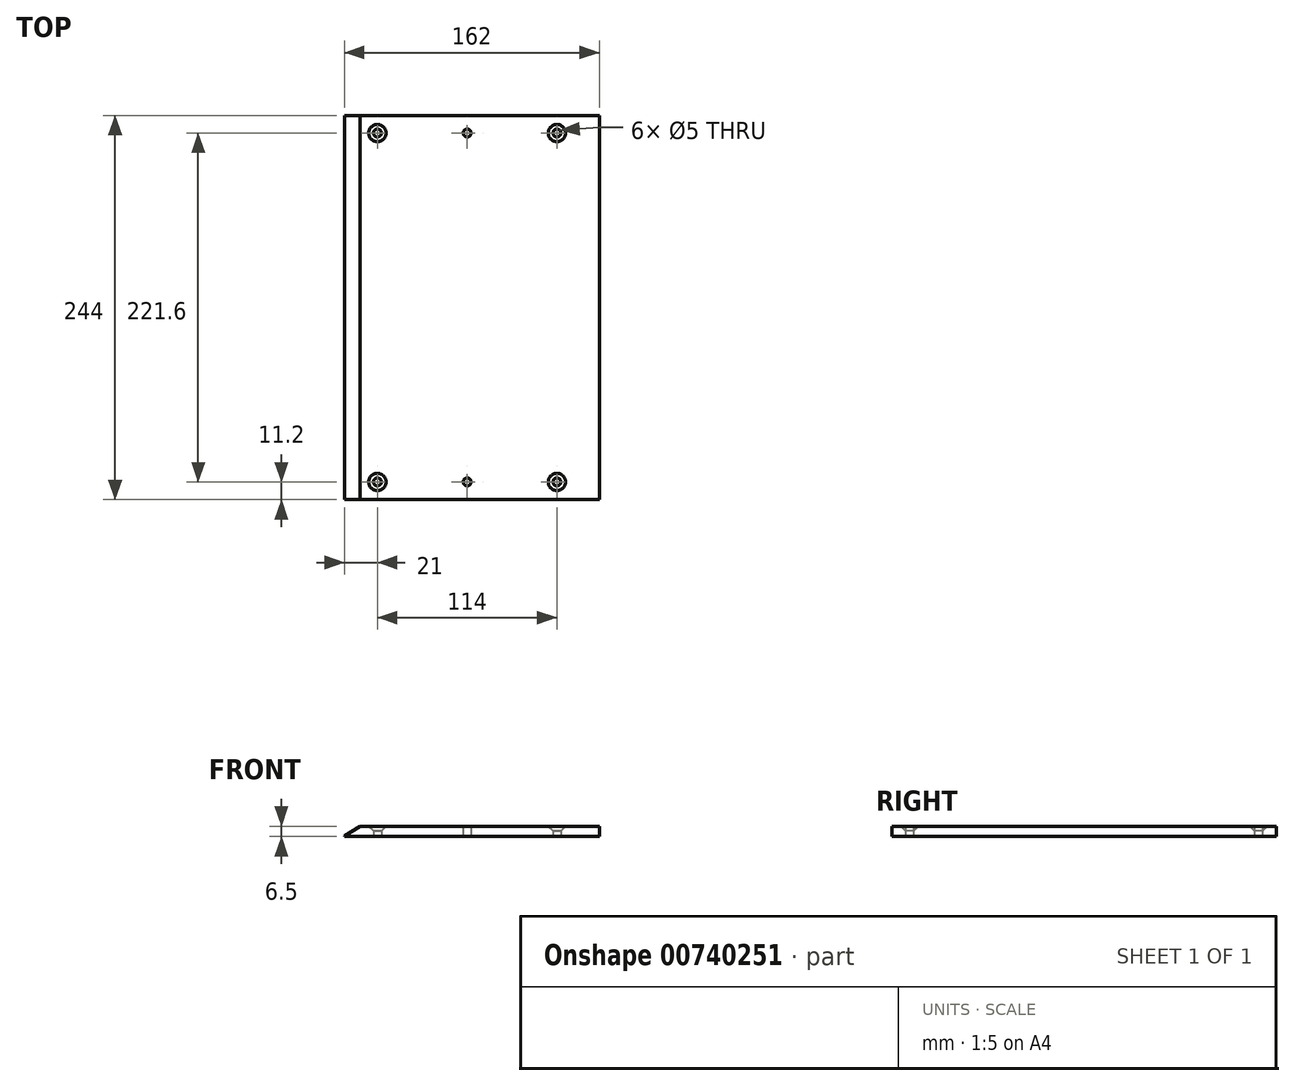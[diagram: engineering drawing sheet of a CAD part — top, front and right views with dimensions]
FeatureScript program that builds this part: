
annotation { "Feature Type Name" : "Feature", "Feature Type Description" : "" }
export const myFeature = defineFeature(function(context is Context, id is Id, definition is map)
    precondition{}
    {
        {
            var Q0;
            Q0=qCreatedBy(makeId("Top.planeOp"),FACE);
            var sketch = newSketch(context, id + "F0", { "sketchPlane" : qUnion([Q0])});
            skLineSegment(sketch, "E0.bottom", {"start": v(-120, 83.5) * mm, "end": v(120, 83.5) * mm});
            skLineSegment(sketch, "E0.top", {"start": v(-120, -83.5) * mm, "end": v(120, -83.5) * mm});
            skLineSegment(sketch, "E0.left", {"start": v(-120, 83.5) * mm, "end": v(-120, -83.5) * mm});
            skLineSegment(sketch, "E0.right", {"start": v(120, 83.5) * mm, "end": v(120, -83.5) * mm});
            skLineSegment(sketch, "E1", {"start": v(-109, 83.5) * mm, "end": v(-109, -83.5) * mm, "construction": true});
            skCircle(sketch, "E2", {"center": v(-109, -56.5) * mm, "radius": 2.5 * mm});
            skCircle(sketch, "E3", {"center": v(-109, -1) * mm, "radius": 2.5 * mm});
            skCircle(sketch, "E4", {"center": v(-109, 57.5) * mm, "radius": 2.5 * mm});
            skCircle(sketch, "E5.MirrorC", {"center": v(109, 57.5) * mm, "radius": 2.5 * mm});
            skCircle(sketch, "E6.MirrorC", {"center": v(109, -1) * mm, "radius": 2.5 * mm});
            skCircle(sketch, "E7.MirrorC", {"center": v(109, -56.5) * mm, "radius": 2.5 * mm});
            skCircle(sketch, "E8", {"center": v(-109, -56.5) * mm, "radius": 5.25 * mm});
            skCircle(sketch, "E9", {"center": v(-109, -1) * mm, "radius": 5.25 * mm});
            skCircle(sketch, "E10", {"center": v(-109, 57.5) * mm, "radius": 5.25 * mm});
            skCircle(sketch, "E11", {"center": v(109, 57.5) * mm, "radius": 5.25 * mm});
            skCircle(sketch, "E12", {"center": v(109, -1) * mm, "radius": 5.25 * mm});
            skCircle(sketch, "E13", {"center": v(109, -56.5) * mm, "radius": 5.25 * mm});
            skSolve(sketch);
        }
        {
            var Q0;
            Q0=qCreatedBy(makeId("Top.planeOp"),FACE);
            var sketch = newSketch(context, id + "F1", { "sketchPlane" : qUnion([Q0])});
            skLineSegment(sketch, "E14.0", {"start": v(-120, 83.5) * mm, "end": v(-120, -83.5) * mm});
            skLineSegment(sketch, "E15.0", {"start": v(-120, 83.5) * mm, "end": v(120, 83.5) * mm});
            skLineSegment(sketch, "E16.0", {"start": v(120, 83.5) * mm, "end": v(120, -83.5) * mm});
            skLineSegment(sketch, "E17.0", {"start": v(-120, -83.5) * mm, "end": v(120, -83.5) * mm});
            skSolve(sketch);
        }
        {
            var Q0;
            Q0 = qSketchRegion(id + "F1", true);
            extrude(context, id + "F2", {"entities" : qUnion([Q0]), "depth" : 6.5 * mm, "offsetDistance" : 25 * mm});
        }
        {
            var Q0;
            Q0=makeQuery(id+"F0.imprint","IMPRINT",FACE,{"disambiguationData":[TD([[makeQuery(id+"F0.imprint","IMPRINT",EDGE,{"derivedFrom":sQuery(id+"F0.wireOp",EDGE,"E0.bottom")}),-1.0]])]});
            var sketch = newSketch(context, id + "F3", { "sketchPlane" : qUnion([Q0])});
            skCircle(sketch, "E18.0", {"center": v(109, -56.5) * mm, "radius": 2.5 * mm, "construction": true});
            skLineSegment(sketch, "E19", {"start": v(110.8, 87.15) * mm, "end": v(110.8, -89.05) * mm, "construction": true});
            skCircle(sketch, "E20", {"center": v(110.8, -56.5) * mm, "radius": 2.5 * mm});
            skCircle(sketch, "E21.0", {"center": v(109, 57.5) * mm, "radius": 2.5 * mm, "construction": true});
            skCircle(sketch, "E22", {"center": v(110.8, 57.5) * mm, "radius": 2.5 * mm});
            skCircle(sketch, "E23.MirrorC", {"center": v(-110.8, -56.5) * mm, "radius": 2.5 * mm});
            skCircle(sketch, "E24.MirrorC", {"center": v(-110.8, 57.5) * mm, "radius": 2.5 * mm});
            skCircle(sketch, "E25", {"center": v(110.8, 0.5) * mm, "radius": 2.5 * mm});
            skCircle(sketch, "E26", {"center": v(-110.8, 0.5) * mm, "radius": 2.5 * mm});
            skLineSegment(sketch, "E27.0.0", {"start": v(-120, 83.5) * mm, "end": v(-120, -83.5) * mm, "construction": true});
            skLineSegment(sketch, "E27.0.1", {"start": v(-120, -83.5) * mm, "end": v(120, -83.5) * mm, "construction": true});
            skLineSegment(sketch, "E27.0.2", {"start": v(120, -83.5) * mm, "end": v(120, 83.5) * mm, "construction": true});
            skLineSegment(sketch, "E27.0.3", {"start": v(120, 83.5) * mm, "end": v(-120, 83.5) * mm, "construction": true});
            skSolve(sketch);
        }
        {
            var Q0;
            Q0 = qSketchRegion(id + "F3", true);
            extrude(context, id + "F4", {"entities" : qUnion([Q0]), "operationType" : NewBodyOperationType.REMOVE, "depth" : 25 * mm, "offsetDistance" : 25 * mm});
        }
        {
            var Q0;
            Q0=makeQuery(id+"F2.opExtrude","CAP_FACE",FACE,{"disambiguationData":[OSD([sQuery(id+"F1.wireOp",EDGE,"E14.0"),sQuery(id+"F1.wireOp",EDGE,"E15.0"),sQuery(id+"F1.wireOp",EDGE,"E16.0"),sQuery(id+"F1.wireOp",EDGE,"E17.0")])],"isStart":false});
            var sketch = newSketch(context, id + "F5", { "sketchPlane" : qUnion([Q0])});
            skCircle(sketch, "E28.0", {"center": v(110.8, -56.5) * mm, "radius": 2.5 * mm, "construction": true});
            skLineSegment(sketch, "E29", {"start": v(120, -29.5) * mm, "end": v(146.96, -29.5) * mm, "construction": true});
            skLineSegment(sketch, "E30", {"start": v(120, -83.5) * mm, "end": v(128.65, -59.63) * mm});
            skLineSegment(sketch, "E31", {"start": v(120, -29.5) * mm, "end": v(128.65, -53.37) * mm});
            skArc(sketch, "E32.trimOffspring", {"start": v(128.65, -59.63) * mm, "mid": v(129.2, -56.5) * mm, "end": v(128.65, -53.37) * mm});
            skCircle(sketch, "E33.0", {"center": v(110.8, 57.5) * mm, "radius": 2.5 * mm, "construction": true});
            skLineSegment(sketch, "E34.trimOffspring", {"start": v(120, -29.5) * mm, "end": v(120, -83.5) * mm});
            skLineSegment(sketch, "E35.0", {"start": v(-120, 83.5) * mm, "end": v(120, 83.5) * mm, "construction": true});
            skLineSegment(sketch, "E36", {"start": v(66.93, -83.5) * mm, "end": v(66.93, 83.5) * mm, "construction": true});
            skLineSegment(sketch, "E37", {"start": v(66.93, 0) * mm, "end": v(30.69, 0) * mm, "construction": true});
            skLineSegment(sketch, "E38.MirrorCS", {"start": v(120, 24.5) * mm, "end": v(120, 78.5) * mm});
            skLineSegment(sketch, "E39.MirrorCS", {"start": v(120, 78.5) * mm, "end": v(128.65, 54.63) * mm});
            skLineSegment(sketch, "E40.MirrorCS", {"start": v(120, 24.5) * mm, "end": v(128.65, 48.37) * mm});
            skArc(sketch, "E41.MirrorCS", {"start": v(128.65, 54.63) * mm, "mid": v(129.2, 51.5) * mm, "end": v(128.65, 48.37) * mm});
            skArc(sketch, "E42.MirrorCS", {"start": v(-128.65, -59.63) * mm, "mid": v(-129.2, -56.5) * mm, "end": v(-128.65, -53.37) * mm});
            skArc(sketch, "E43.MirrorCS", {"start": v(-128.65, 54.63) * mm, "mid": v(-129.2, 51.5) * mm, "end": v(-128.65, 48.37) * mm});
            skLineSegment(sketch, "E44.MirrorCS", {"start": v(-120, 24.5) * mm, "end": v(-128.65, 48.37) * mm});
            skLineSegment(sketch, "E45.MirrorCS", {"start": v(-120, -29.5) * mm, "end": v(-120, -83.5) * mm});
            skLineSegment(sketch, "E46.MirrorCS", {"start": v(-120, 78.5) * mm, "end": v(-128.65, 54.63) * mm});
            skLineSegment(sketch, "E47.MirrorCS", {"start": v(-120, -29.5) * mm, "end": v(-128.65, -53.37) * mm});
            skLineSegment(sketch, "E48.MirrorCS", {"start": v(-120, 24.5) * mm, "end": v(-120, 78.5) * mm});
            skLineSegment(sketch, "E49.MirrorCS", {"start": v(-120, -83.5) * mm, "end": v(-128.65, -59.63) * mm});
            skLineSegment(sketch, "E50", {"start": v(-126.82, 24.5) * mm, "end": v(132.7, 24.5) * mm, "construction": true});
            skSolve(sketch);
        }
        {
            var Q0;
            Q0=makeQuery(id+"F4.boolean.opBoolean","INTERSECT",EDGE,{"derivedFrom":[makeQuery(id+"F2.opExtrude","CAP_FACE",FACE,{"disambiguationData":[OSD([sQuery(id+"F1.wireOp",EDGE,"E14.0"),sQuery(id+"F1.wireOp",EDGE,"E15.0"),sQuery(id+"F1.wireOp",EDGE,"E16.0"),sQuery(id+"F1.wireOp",EDGE,"E17.0")])],"isStart":false}),makeQuery(id+"F4.opExtrude","SWEPT_FACE",FACE,{"disambiguationData":[OSD([sQuery(id+"F3.wireOp",EDGE,"E24.MirrorC")])]})]});
            var Q1;
            Q1=makeQuery(id+"F4.boolean.opBoolean","INTERSECT",EDGE,{"derivedFrom":[makeQuery(id+"F2.opExtrude","CAP_FACE",FACE,{"disambiguationData":[OSD([sQuery(id+"F1.wireOp",EDGE,"E14.0"),sQuery(id+"F1.wireOp",EDGE,"E15.0"),sQuery(id+"F1.wireOp",EDGE,"E16.0"),sQuery(id+"F1.wireOp",EDGE,"E17.0")])],"isStart":false}),makeQuery(id+"F4.opExtrude","SWEPT_FACE",FACE,{"disambiguationData":[OSD([sQuery(id+"F3.wireOp",EDGE,"9799492e-2de3-4028-b242-5b233e700d641.MirrorC")])]})]});
            var Q2;
            Q2=makeQuery(id+"F4.boolean.opBoolean","INTERSECT",EDGE,{"derivedFrom":[makeQuery(id+"F2.opExtrude","CAP_FACE",FACE,{"disambiguationData":[OSD([sQuery(id+"F1.wireOp",EDGE,"E14.0"),sQuery(id+"F1.wireOp",EDGE,"E15.0"),sQuery(id+"F1.wireOp",EDGE,"E16.0"),sQuery(id+"F1.wireOp",EDGE,"E17.0")])],"isStart":false}),makeQuery(id+"F4.opExtrude","SWEPT_FACE",FACE,{"disambiguationData":[OSD([sQuery(id+"F3.wireOp",EDGE,"E23.MirrorC")])]})]});
            var Q3;
            Q3=makeQuery(id+"F4.boolean.opBoolean","INTERSECT",EDGE,{"derivedFrom":[makeQuery(id+"F2.opExtrude","CAP_FACE",FACE,{"disambiguationData":[OSD([sQuery(id+"F1.wireOp",EDGE,"E14.0"),sQuery(id+"F1.wireOp",EDGE,"E15.0"),sQuery(id+"F1.wireOp",EDGE,"E16.0"),sQuery(id+"F1.wireOp",EDGE,"E17.0")])],"isStart":false}),makeQuery(id+"F4.opExtrude","SWEPT_FACE",FACE,{"disambiguationData":[OSD([sQuery(id+"F3.wireOp",EDGE,"E20")])]})]});
            var Q4;
            Q4=makeQuery(id+"F4.boolean.opBoolean","INTERSECT",EDGE,{"derivedFrom":[makeQuery(id+"F2.opExtrude","CAP_FACE",FACE,{"disambiguationData":[OSD([sQuery(id+"F1.wireOp",EDGE,"E14.0"),sQuery(id+"F1.wireOp",EDGE,"E15.0"),sQuery(id+"F1.wireOp",EDGE,"E16.0"),sQuery(id+"F1.wireOp",EDGE,"E17.0")])],"isStart":false}),makeQuery(id+"F4.opExtrude","SWEPT_FACE",FACE,{"disambiguationData":[OSD([sQuery(id+"F3.wireOp",EDGE,"IaooAQb2-GWYG-qIhj-kNX2-8eC1LoJ4aaHl")])]})]});
            var Q5;
            Q5=makeQuery(id+"F4.boolean.opBoolean","INTERSECT",EDGE,{"derivedFrom":[makeQuery(id+"F2.opExtrude","CAP_FACE",FACE,{"disambiguationData":[OSD([sQuery(id+"F1.wireOp",EDGE,"E14.0"),sQuery(id+"F1.wireOp",EDGE,"E15.0"),sQuery(id+"F1.wireOp",EDGE,"E16.0"),sQuery(id+"F1.wireOp",EDGE,"E17.0")])],"isStart":false}),makeQuery(id+"F4.opExtrude","SWEPT_FACE",FACE,{"disambiguationData":[OSD([sQuery(id+"F3.wireOp",EDGE,"E22")])]})]});
            chamfer(context, id + "F6", {"entities" : qUnion([Q0, Q1, Q2, Q3, Q4, Q5]), "width" : 3 * mm, "tangentPropagation" : true});
        }
        {
            var Q0;
            {var subQ0=sQuery(id+"F1.wireOp",EDGE,"E17.0");var subQ1=sQuery(id+"F1.wireOp",EDGE,"E16.0");var subQ2=sQuery(id+"F1.wireOp",EDGE,"E15.0");var subQ3=sQuery(id+"F1.wireOp",EDGE,"E14.0");Q0=makeQuery(id+"FmiwI8BXhnqw8v8_1.boolean.opBoolean","MERGE",FACE,{"derivedFrom":[makeQuery(id+"F2.opExtrude","CAP_FACE",FACE,{"disambiguationData":[OSD([subQ3,subQ2,subQ1,subQ0])],"isStart":true}),makeQuery(id+"FmiwI8BXhnqw8v8_1.opExtrude","CAP_FACE",FACE,{"disambiguationData":[OSD([subQ3,subQ2,subQ1,subQ0]),OD(0.0)],"isStart":false}),makeQuery(id+"FmiwI8BXhnqw8v8_1.opExtrude","CAP_FACE",FACE,{"disambiguationData":[OSD([subQ3,subQ2,subQ1,subQ0]),OD(1.0)],"isStart":false}),makeQuery(id+"FmiwI8BXhnqw8v8_1.opExtrude","CAP_FACE",FACE,{"disambiguationData":[OSD([subQ3,subQ2,subQ1,subQ0]),OD(2.0)],"isStart":false}),makeQuery(id+"FmiwI8BXhnqw8v8_1.opExtrude","CAP_FACE",FACE,{"disambiguationData":[OSD([subQ3,subQ2,subQ1,subQ0]),OD(3.0)],"isStart":false})]});}
            var sketch = newSketch(context, id + "F7", { "sketchPlane" : qUnion([Q0])});
            skLineSegment(sketch, "E51.0", {"start": v(-121.45, -78.5) * mm, "end": v(121.45, -78.5) * mm});
            skPoint(sketch, "E52.orphan", {"position": v(-128.65, -54.63) * mm});
            skPoint(sketch, "E53.orphan", {"position": v(128.65, -54.63) * mm});
            skLineSegment(sketch, "E54", {"start": v(-121.45, -78.5) * mm, "end": v(-148.95, -97.63) * mm});
            skLineSegment(sketch, "E55", {"start": v(-148.95, -97.63) * mm, "end": v(134.45, -97.63) * mm});
            skLineSegment(sketch, "E56", {"start": v(134.45, -97.63) * mm, "end": v(121.45, -78.5) * mm});
            skLineSegment(sketch, "E57.0", {"start": v(-120, -83.5) * mm, "end": v(120, -83.5) * mm, "construction": true});
            skSolve(sketch);
        }
        {
            var Q0;
            Q0 = qSketchRegion(id + "F7", true);
            extrude(context, id + "F8", {"entities" : qUnion([Q0]), "operationType" : NewBodyOperationType.REMOVE, "oppositeDirection" : true, "depth" : 25 * mm, "offsetDistance" : 25 * mm});
        }
        {
            var Q0;
            Q0=makeQuery(id+"F2.opExtrude","SWEPT_FACE",FACE,{"disambiguationData":[OSD([sQuery(id+"F1.wireOp",EDGE,"E14.0")])]});
            extrude(context, id + "F9", {"entities" : qUnion([Q0]), "operationType" : NewBodyOperationType.ADD, "depth" : 2 * mm, "offsetDistance" : 25 * mm});
        }
        {
            var Q0;
            Q0=makeQuery(id+"F2.opExtrude","SWEPT_FACE",FACE,{"disambiguationData":[OSD([sQuery(id+"F1.wireOp",EDGE,"E16.0")])]});
            extrude(context, id + "F10", {"entities" : qUnion([Q0]), "operationType" : NewBodyOperationType.ADD, "depth" : 2 * mm, "offsetDistance" : 25 * mm});
        }
        {
            var Q0;
            Q0=makeQuery(id+"F8.boolean.opBoolean","INTERSECT",EDGE,{"derivedFrom":[makeQuery(id+"FmiwI8BXhnqw8v8_1.boolean.opBoolean","MERGE",FACE,{"derivedFrom":[makeQuery(id+"F2.opExtrude","CAP_FACE",FACE,{"disambiguationData":[OSD([sQuery(id+"F1.wireOp",EDGE,"E14.0"),sQuery(id+"F1.wireOp",EDGE,"E15.0"),sQuery(id+"F1.wireOp",EDGE,"E16.0"),sQuery(id+"F1.wireOp",EDGE,"E17.0")])],"isStart":false}),makeQuery(id+"FmiwI8BXhnqw8v8_1.opExtrude","CAP_FACE",FACE,{"disambiguationData":[OSD([sQuery(id+"F5.wireOp",EDGE,"E30"),sQuery(id+"F5.wireOp",EDGE,"E31"),sQuery(id+"F5.wireOp",EDGE,"E32.trimOffspring"),sQuery(id+"F5.wireOp",EDGE,"E34.trimOffspring")])],"isStart":true}),makeQuery(id+"FmiwI8BXhnqw8v8_1.opExtrude","CAP_FACE",FACE,{"disambiguationData":[OSD([sQuery(id+"F5.wireOp",EDGE,"E38.MirrorCS"),sQuery(id+"F5.wireOp",EDGE,"E39.MirrorCS"),sQuery(id+"F5.wireOp",EDGE,"E40.MirrorCS"),sQuery(id+"F5.wireOp",EDGE,"E41.MirrorCS")])],"isStart":true}),makeQuery(id+"FmiwI8BXhnqw8v8_1.opExtrude","CAP_FACE",FACE,{"disambiguationData":[OSD([sQuery(id+"F5.wireOp",EDGE,"E42.MirrorCS"),sQuery(id+"F5.wireOp",EDGE,"E45.MirrorCS"),sQuery(id+"F5.wireOp",EDGE,"E47.MirrorCS"),sQuery(id+"F5.wireOp",EDGE,"E49.MirrorCS")])],"isStart":true}),makeQuery(id+"FmiwI8BXhnqw8v8_1.opExtrude","CAP_FACE",FACE,{"disambiguationData":[OSD([sQuery(id+"F5.wireOp",EDGE,"E43.MirrorCS"),sQuery(id+"F5.wireOp",EDGE,"E44.MirrorCS"),sQuery(id+"F5.wireOp",EDGE,"E46.MirrorCS"),sQuery(id+"F5.wireOp",EDGE,"E48.MirrorCS")])],"isStart":true})]}),makeQuery(id+"F8.opExtrude","SWEPT_FACE",FACE,{"disambiguationData":[OSD([sQuery(id+"F7.wireOp",EDGE,"E51.0")])]})]});
            chamfer(context, id + "F11", {"entities" : qUnion([Q0]), "chamferType" : ChamferType.TWO_OFFSETS, "width1" : 6 * mm, "oppositeDirection" : true, "width2" : 10 * mm, "tangentPropagation" : true});
        }
        {
            var Q0;
            Q0=qCreatedBy(makeId("Right.planeOp"),FACE);
            var sketch = newSketch(context, id + "F12", { "sketchPlane" : qUnion([Q0])});
            skLineSegment(sketch, "E58", {"start": v(0, 0) * mm, "end": v(0, 105.61) * mm});
            skSolve(sketch);
        }
        {
            var Q0;
            Q0=makeQuery(id+"F2.opExtrude","SWEPT_BODY",BODY,{"disambiguationData":[OSD([sQuery(id+"F1.wireOp",EDGE,"E14.0"),sQuery(id+"F1.wireOp",EDGE,"E15.0"),sQuery(id+"F1.wireOp",EDGE,"E16.0"),sQuery(id+"F1.wireOp",EDGE,"E17.0")])]});
            var Q1;
            Q1=sQuery(id+"F12.wireOp",EDGE,"E58");
            transform(context, id + "F13", {"entities" : qUnion([Q0]), "transformType" : TransformType.ROTATION, "transformAxis" : qUnion([Q1]), "angle" : 90 * degree, "makeCopy" : false});
        }
    });
